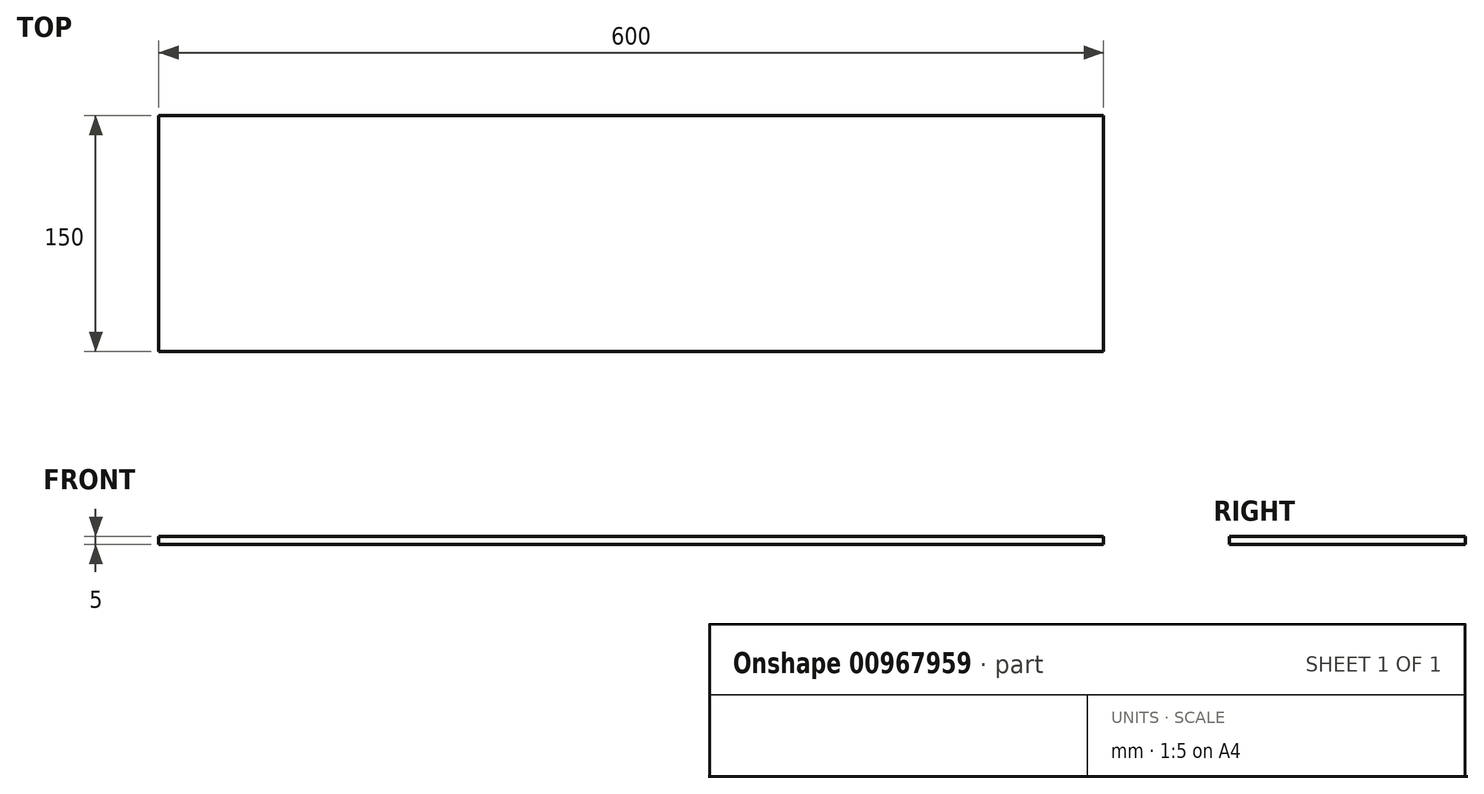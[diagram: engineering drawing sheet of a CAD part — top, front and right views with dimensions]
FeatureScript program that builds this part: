
annotation { "Feature Type Name" : "Feature", "Feature Type Description" : "" }
export const myFeature = defineFeature(function(context is Context, id is Id, definition is map)
    precondition{}
    {
        {
            var Q0;
            Q0=qCreatedBy(makeId("Top.planeOp"),FACE);
            var sketch = newSketch(context, id + "F0", { "sketchPlane" : qUnion([Q0])});
            skLineSegment(sketch, "E0.bottom", {"start": v(300, -75) * mm, "end": v(-300, -75) * mm});
            skLineSegment(sketch, "E0.top", {"start": v(300, 75) * mm, "end": v(-300, 75) * mm});
            skLineSegment(sketch, "E0.left", {"start": v(300, -75) * mm, "end": v(300, 75) * mm});
            skLineSegment(sketch, "E0.right", {"start": v(-300, -75) * mm, "end": v(-300, 75) * mm});
            skPoint(sketch, "E0.middle", {"position": v(0, 0) * mm});
            skSolve(sketch);
        }
        {
            var Q0;
            Q0 = qSketchRegion(id + "F0", true);
            extrude(context, id + "F1", {"entities" : qUnion([Q0]), "depth" : 5 * mm, "offsetDistance" : 25 * mm});
        }
    });
